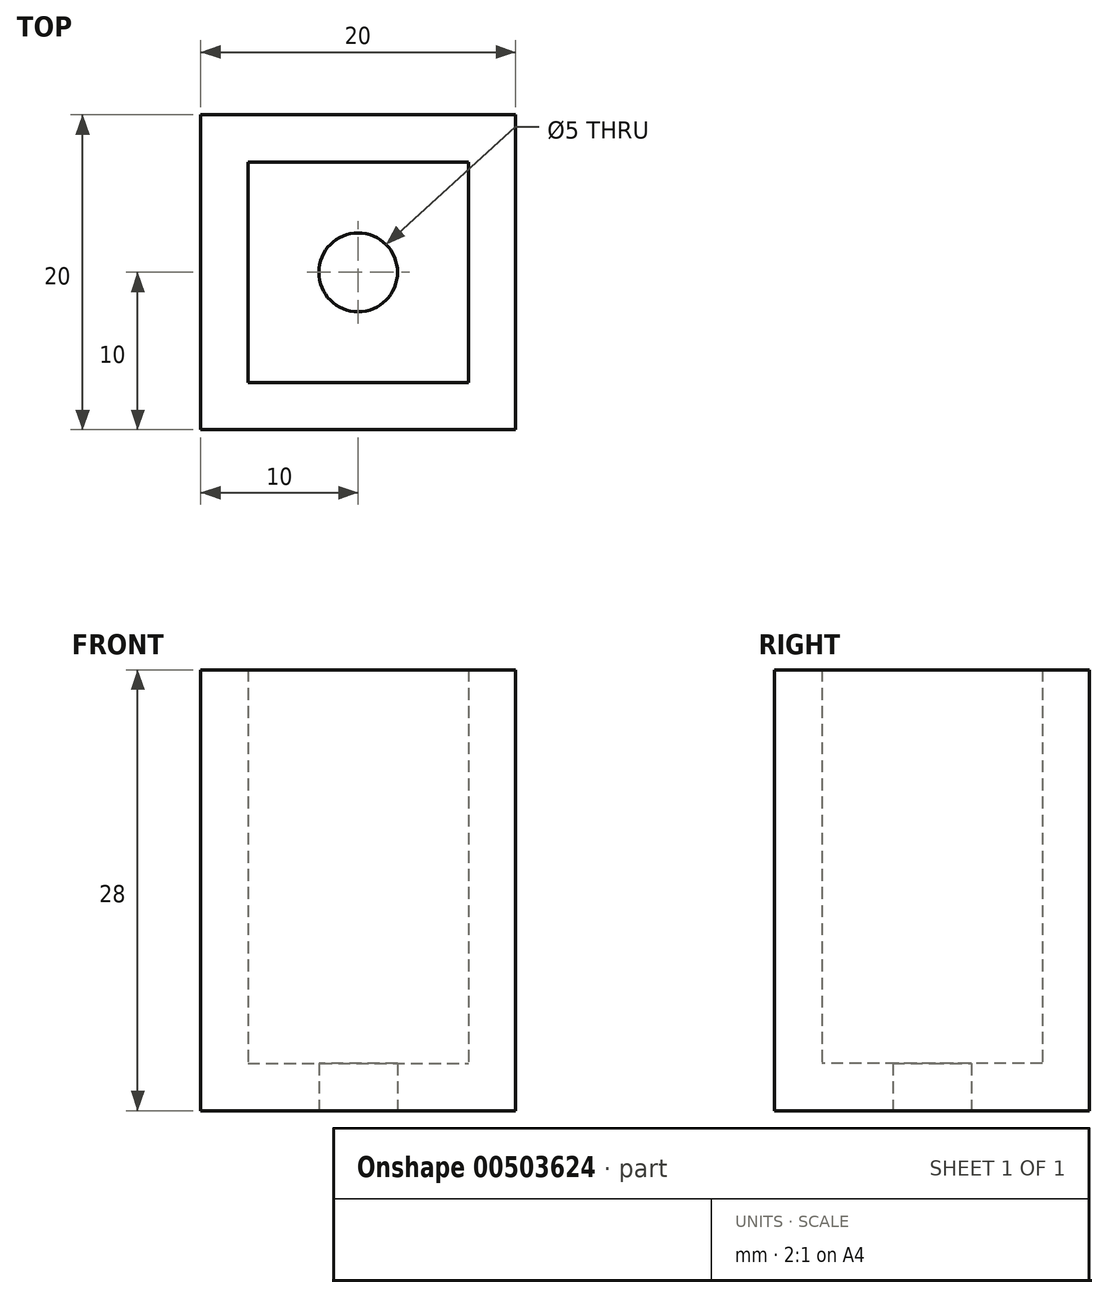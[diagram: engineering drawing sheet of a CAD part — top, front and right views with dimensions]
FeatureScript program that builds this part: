
annotation { "Feature Type Name" : "Feature", "Feature Type Description" : "" }
export const myFeature = defineFeature(function(context is Context, id is Id, definition is map)
    precondition{}
    {
        {
            var Q0;
            Q0=qCreatedBy(makeId("Top.planeOp"),FACE);
            var sketch = newSketch(context, id + "F0", { "sketchPlane" : qUnion([Q0])});
            skLineSegment(sketch, "E0.bottom", {"start": v(-10, 10) * mm, "end": v(10, 10) * mm});
            skLineSegment(sketch, "E0.top", {"start": v(-10, -10) * mm, "end": v(10, -10) * mm});
            skLineSegment(sketch, "E0.left", {"start": v(-10, 10) * mm, "end": v(-10, -10) * mm});
            skLineSegment(sketch, "E0.right", {"start": v(10, 10) * mm, "end": v(10, -10) * mm});
            skPoint(sketch, "E0.middle", {"position": v(0, 0) * mm});
            skLineSegment(sketch, "E1.0", {"start": v(-7, 7) * mm, "end": v(7, 7) * mm});
            skLineSegment(sketch, "E1.1", {"start": v(-7, 7) * mm, "end": v(-7, -7) * mm});
            skLineSegment(sketch, "E1.2", {"start": v(-7, -7) * mm, "end": v(7, -7) * mm});
            skLineSegment(sketch, "E1.3", {"start": v(7, 7) * mm, "end": v(7, -7) * mm});
            skCircle(sketch, "E2", {"center": v(0, 0) * mm, "radius": 2.5 * mm});
            skSolve(sketch);
        }
        {
            var Q0;
            Q0=makeQuery(id+"F0.imprint","IMPRINT",FACE,{"disambiguationData":[TD([[makeQuery(id+"F0.imprint","IMPRINT",EDGE,{"derivedFrom":sQuery(id+"F0.wireOp",EDGE,"E0.bottom")}),-1.0]])]});
            extrude(context, id + "F1", {"entities" : qUnion([Q0]), "depth" : 28 * mm});
        }
        {
            var Q0;
            Q0=makeQuery(id+"F0.imprint","IMPRINT",FACE,{"disambiguationData":[TD([[makeQuery(id+"F0.imprint","IMPRINT",EDGE,{"derivedFrom":sQuery(id+"F0.wireOp",EDGE,"E1.0")}),-1.0]])]});
            extrude(context, id + "F2", {"entities" : qUnion([Q0]), "operationType" : NewBodyOperationType.ADD, "depth" : 3 * mm});
        }
    });
